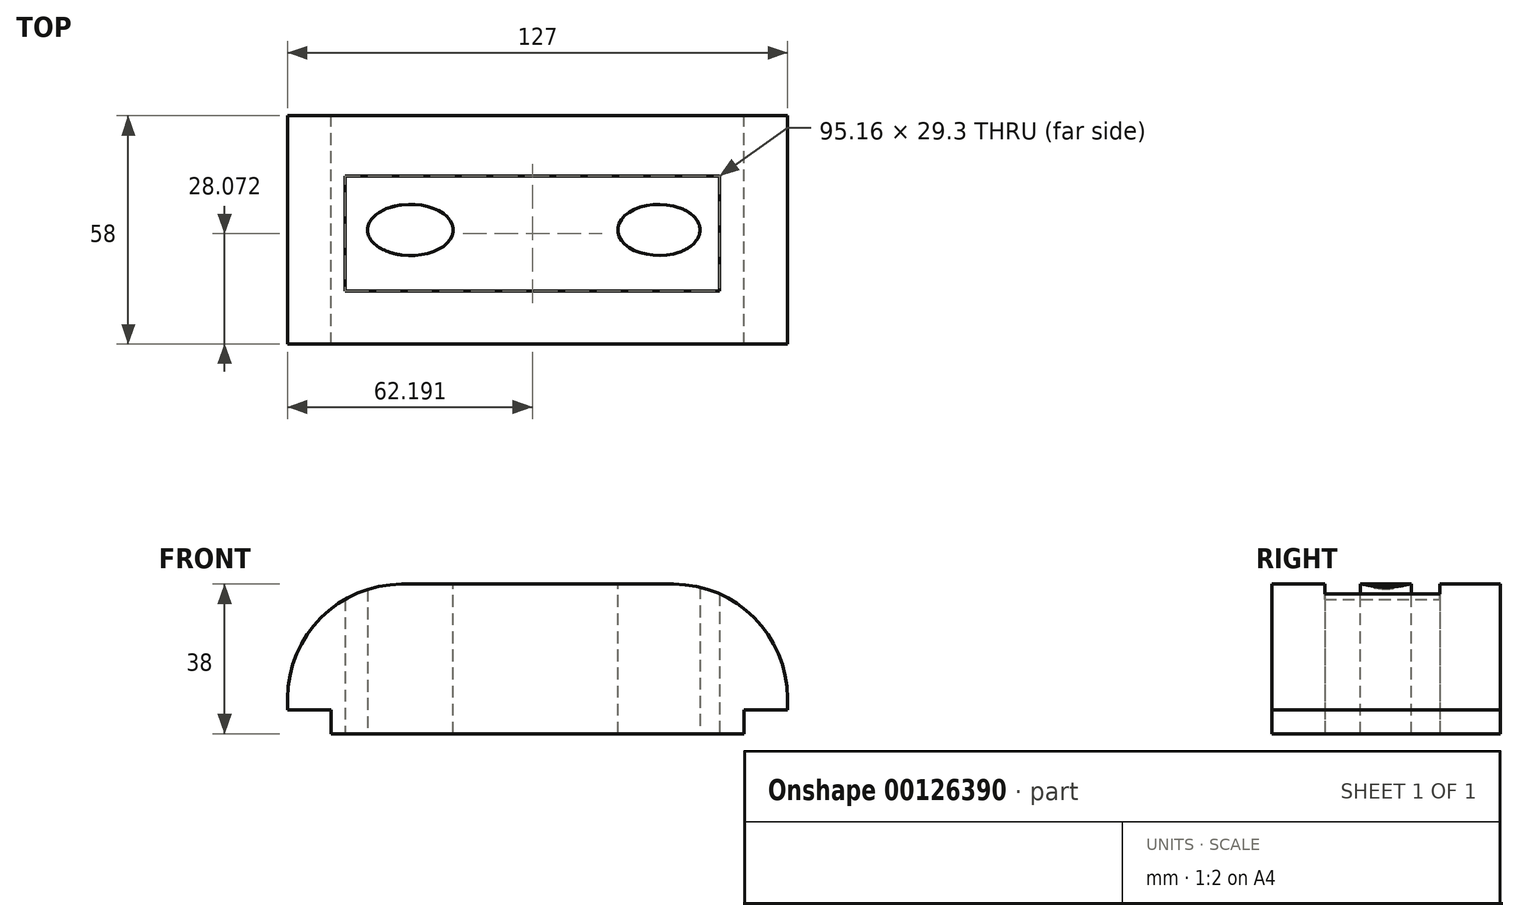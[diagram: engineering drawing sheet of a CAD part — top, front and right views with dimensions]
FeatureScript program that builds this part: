
annotation { "Feature Type Name" : "Feature", "Feature Type Description" : "" }
export const myFeature = defineFeature(function(context is Context, id is Id, definition is map)
    precondition{}
    {
        {
            var Q0;
            Q0=qCreatedBy(makeId("Front.planeOp"),FACE);
            var sketch = newSketch(context, id + "F0", { "sketchPlane" : qUnion([Q0])});
            skLineSegment(sketch, "E0.bottom", {"start": v(0, 0) * mm, "end": v(127, 0) * mm});
            skLineSegment(sketch, "E0.top", {"start": v(29, 38) * mm, "end": v(98, 38) * mm});
            skLineSegment(sketch, "E0.left", {"start": v(0, 0) * mm, "end": v(0, 9) * mm});
            skLineSegment(sketch, "E0.right", {"start": v(127, 0) * mm, "end": v(127, 9) * mm});
            skPoint(sketch, "E1.visualSharp", {"position": v(0, 38) * mm});
            skArc(sketch, "E1.filletArc", {"start": v(29, 38) * mm, "mid": v(8.5, 29.5) * mm, "end": v(0, 9) * mm});
            skPoint(sketch, "E2.visualSharp", {"position": v(127, 38) * mm});
            skArc(sketch, "E2.filletArc", {"start": v(127, 9) * mm, "mid": v(118.5, 29.5) * mm, "end": v(98, 38) * mm});
            skSolve(sketch);
        }
        {
            var Q0;
            Q0 = qSketchRegion(id + "F0", true);
            extrude(context, id + "F1", {"entities" : qUnion([Q0]), "depth" : 58 * mm});
        }
        {
            var Q0;
            Q0=qCreatedBy(makeId("Front.planeOp"),FACE);
            var sketch = newSketch(context, id + "F2", { "sketchPlane" : qUnion([Q0])});
            skLineSegment(sketch, "E3.bottom", {"start": v(116, 0) * mm, "end": v(127, 0) * mm});
            skLineSegment(sketch, "E3.top", {"start": v(116, 6) * mm, "end": v(127, 6) * mm});
            skLineSegment(sketch, "E3.left", {"start": v(116, 0) * mm, "end": v(116, 6) * mm});
            skLineSegment(sketch, "E3.right", {"start": v(127, 0) * mm, "end": v(127, 6) * mm});
            skLineSegment(sketch, "E4.bottom", {"start": v(0, 0) * mm, "end": v(11, 0) * mm});
            skLineSegment(sketch, "E4.top", {"start": v(0, 6) * mm, "end": v(11, 6) * mm});
            skLineSegment(sketch, "E4.left", {"start": v(0, 0) * mm, "end": v(0, 6) * mm});
            skLineSegment(sketch, "E4.right", {"start": v(11, 0) * mm, "end": v(11, 6) * mm});
            skSolve(sketch);
        }
        {
            var Q0;
            Q0 = qSketchRegion(id + "F2", true);
            extrude(context, id + "F3", {"entities" : qUnion([Q0]), "operationType" : NewBodyOperationType.REMOVE, "depth" : 58 * mm});
        }
        {
            var Q0;
            Q0=qCreatedBy(makeId("Top.planeOp"),FACE);
            var sketch = newSketch(context, id + "F4", { "sketchPlane" : qUnion([Q0])});
            skLineSegment(sketch, "E5.bottom", {"start": v(14.61, -15.28) * mm, "end": v(109.77, -15.28) * mm});
            skLineSegment(sketch, "E5.top", {"start": v(14.61, -44.58) * mm, "end": v(109.77, -44.58) * mm});
            skLineSegment(sketch, "E5.left", {"start": v(14.61, -15.28) * mm, "end": v(14.61, -44.58) * mm});
            skLineSegment(sketch, "E5.right", {"start": v(109.77, -15.28) * mm, "end": v(109.77, -44.58) * mm});
            skEllipse(sketch, "E6", {"center": v(31.2, -29) * mm, "majorRadius": 10.9 * mm, "minorRadius": 6.5 * mm, "majorAxis": v(-1, 0)});
            skEllipse(sketch, "E7", {"center": v(94.33, -29) * mm, "majorRadius": 10.45 * mm, "minorRadius": 6.5 * mm, "majorAxis": v(1, 0)});
            skLineSegment(sketch, "E8.bottom", {"start": v(0, 0) * mm, "end": v(127, 0) * mm, "construction": true});
            skLineSegment(sketch, "E8.top", {"start": v(0, -58) * mm, "end": v(127, -58) * mm, "construction": true});
            skLineSegment(sketch, "E8.left", {"start": v(0, 0) * mm, "end": v(0, -58) * mm, "construction": true});
            skLineSegment(sketch, "E8.right", {"start": v(127, 0) * mm, "end": v(127, -58) * mm, "construction": true});
            skLineSegment(sketch, "E9", {"start": v(0, -29) * mm, "end": v(127, -29) * mm, "construction": true});
            skLineSegment(sketch, "E10", {"start": v(61.14, 0) * mm, "end": v(61.14, -58) * mm, "construction": true});
            skPoint(sketch, "E11", {"position": v(94.33, -22.5) * mm});
            skPoint(sketch, "E12", {"position": v(31.2, -22.5) * mm});
            skPoint(sketch, "E13", {"position": v(27.7, -29) * mm});
            skPoint(sketch, "E14", {"position": v(33.92, -29) * mm});
            skPoint(sketch, "E15", {"position": v(97, -29) * mm});
            skPoint(sketch, "E16", {"position": v(102, -29) * mm});
            skSolve(sketch);
        }
        {
            var Q0;
            Q0 = qSketchRegion(id + "F4", true);
            extrude(context, id + "F5", {"entities" : qUnion([Q0]), "operationType" : NewBodyOperationType.REMOVE, "endBound" : BoundingType.THROUGH_ALL, "depth" : 25 * mm});
        }
    });
